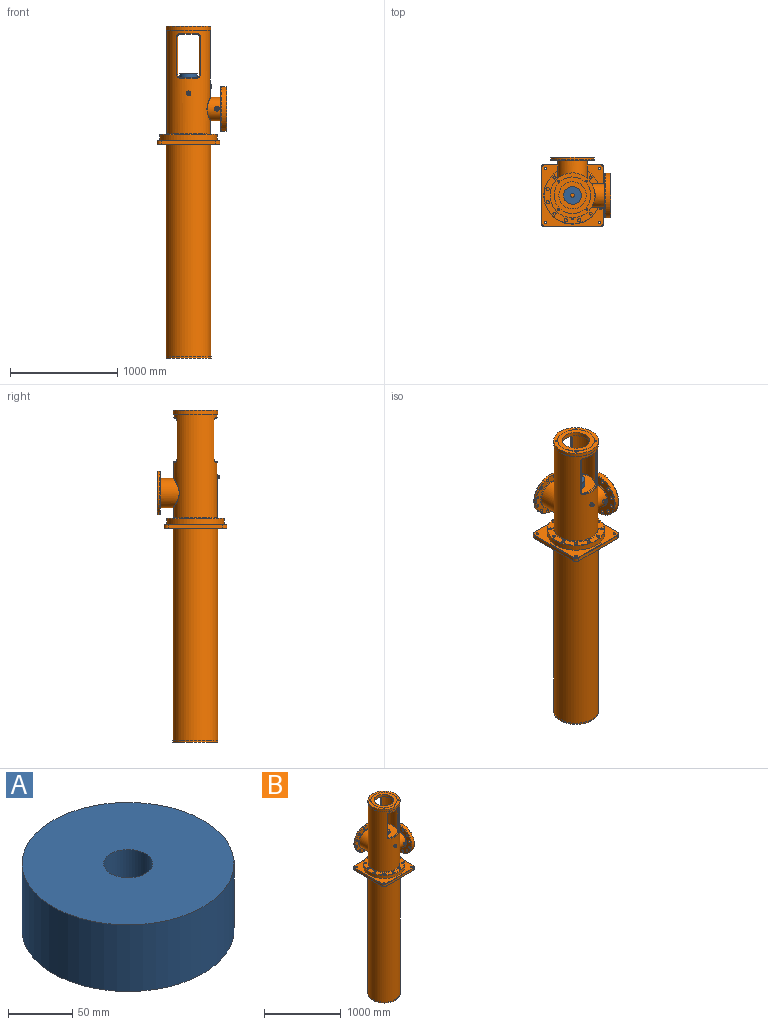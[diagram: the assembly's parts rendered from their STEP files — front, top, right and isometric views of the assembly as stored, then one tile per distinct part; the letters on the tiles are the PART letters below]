
ASSEMBLY  parts=2 mates=1
PART A: 4 faces, bbox 165.1x165.1x63.5 mm
  f0: cylinder r=19.05mm len=63.5mm, axis (0,0,-1), area 7600.6mm2, adj f2,f3
  f1: cylinder r=82.55mm len=165.1mm, axis (0,0,-1), area 32936mm2, adj f2,f3
  f2: plane 165.1x165.1mm, normal (0,0,1), area 20268.3mm2, adj f0,f1
  f3: plane 165.1x165.1mm, normal (0,0,-1), area 20268.3mm2, adj f0,f1
PART B: 185 faces, bbox 649.3x649.3x3098.8 mm
  f0: plane 194.31x194.31mm, normal (1,0,0), area 193.5mm2, adj f18,f177
  f1: cylinder r=127mm len=254mm, axis (0,1,0), area 157545.1mm2, adj f9,f181
  f2: cylinder r=203.2mm len=964.44mm, axis (0,0,-1), area 929917.2mm2, adj f35,f55,f56,f57,f58,f59,f60,f61
  f3: cylinder r=209.55mm len=419.1mm, axis (0,0,-1), area 45816.5mm2, adj f15,f154
  f4: plane 342.9x342.9mm, normal (0,0,1), area 41676.7mm2, adj f14,f153
  f5: cylinder r=12.7mm len=25.4mm, axis (0,1,0), area 1059.8mm2, adj f149,f151
  f6: cylinder r=7.3mm len=25.53mm, axis (0,-1,0), area 1168.4mm2, adj f7,f8
  f7: plane 19.05x19.05mm, normal (0,-1,0), area 117.5mm2, adj f6,f151
  f8: cylinder r=203.2mm len=14.61mm, axis (0,0,-1), area 167.6mm2, adj f6
  f9: cylinder r=184.15mm len=571.5mm, axis (0,0,-1), area 576329.1mm2, adj f1,f18,f74,f184
  f10: cylinder r=109.54mm len=219.08mm, axis (1,0,0), area 70763.1mm2, adj f32,f35,f150
  f11: plane 528.32x528.32mm, normal (0,0,1), area 75242.3mm2, adj f55,f75,f76,f77,f78,f79,f80,f81
  f12: cylinder r=184.15mm len=459.74mm, axis (0,0,-1), area 358288.8mm2, adj f36,f37,f38,f39,f40,f41,f42,f43
  f13: plane 358.14x358.14mm, normal (0,0,-1), area 50067.8mm2, adj f14,f54
  f14: cylinder r=127mm len=254mm, axis (0,0,-1), area 30402.4mm2, adj f4,f13
  f15: plane 419.1x419.1mm, normal (0,0,-1), area 1667.1mm2, adj f3,f56
  f16: cylinder r=209.55mm len=419.1mm, axis (1,0,0), area 57855.9mm2, adj f33,f34
  f17: plane 408.94x408.94mm, normal (-1,0,0), area 80571.2mm2, adj f20,f21,f22,f23,f24,f25,f26,f27
  f18: cylinder r=96.84mm len=198.97mm, axis (1,0,0), area 112354.4mm2, adj f0,f9,f148
  f19: plane 408.94x408.94mm, normal (1,0,0), area 64694.2mm2, adj f20,f21,f22,f23,f24,f25,f26,f27
  f20: cylinder r=15.88mm len=54.1mm, axis (1,0,0), area 5396.4mm2, adj f17,f19
  f21: cylinder r=15.88mm len=54.1mm, axis (1,0,0), area 5396.4mm2, adj f17,f19
  f22: cylinder r=15.88mm len=54.1mm, axis (1,0,0), area 5396.4mm2, adj f17,f19
  f23: cylinder r=15.88mm len=54.1mm, axis (1,0,0), area 5396.4mm2, adj f17,f19
  f24: cylinder r=15.88mm len=54.1mm, axis (1,0,0), area 5396.4mm2, adj f17,f19
  f25: cylinder r=15.88mm len=54.1mm, axis (1,0,0), area 5396.4mm2, adj f17,f19
  f26: cylinder r=15.88mm len=54.1mm, axis (1,0,0), area 5396.4mm2, adj f17,f19
  f27: cylinder r=15.88mm len=54.1mm, axis (1,0,0), area 5396.4mm2, adj f17,f19
  f28: cylinder r=15.88mm len=54.1mm, axis (1,0,0), area 5396.4mm2, adj f17,f19
  f29: cylinder r=15.88mm len=54.1mm, axis (1,0,0), area 5396.4mm2, adj f17,f19
  f30: cylinder r=15.88mm len=54.1mm, axis (1,0,0), area 5396.4mm2, adj f17,f19
  f31: cylinder r=15.88mm len=54.1mm, axis (1,0,0), area 5396.4mm2, adj f17,f19
  f32: torus R=114.62mm, axis (1,0,0), area 5584.5mm2, adj f10,f17
  f33: torus R=204.47mm, axis (1,0,0), area 10413.8mm2, adj f16,f19
  f34: torus R=204.47mm, axis (1,0,0), area 10413.8mm2, adj f16,f17
  f35: bspline ~229.29x223.71mm, area 4645.6mm2, adj f2,f10
  f36: cylinder r=25.4mm len=29.29mm, axis (0,-1,0), area 564.4mm2, adj f12,f37,f43,f67
  f37: plane 355.6x13.36mm, normal (1,0,0), area 4750.8mm2, adj f12,f36,f38,f65
  f38: cylinder r=25.4mm len=29.29mm, axis (0,-1,0), area 564.4mm2, adj f12,f37,f39,f66
  f39: plane 152.4x30.48mm, normal (0,0,-1), area 2190mm2, adj f12,f38,f40,f68
  f40: cylinder r=25.4mm len=29.29mm, axis (0,-1,0), area 564.4mm2, adj f12,f39,f41,f70
  f41: plane 355.6x13.36mm, normal (-1,0,0), area 4750.8mm2, adj f12,f40,f42,f72
  f42: cylinder r=25.4mm len=29.29mm, axis (0,-1,0), area 564.4mm2, adj f12,f41,f43,f71
  f43: plane 152.4x30.48mm, normal (0,0,1), area 2190mm2, adj f12,f36,f42,f69
  f44: plane 152.4x30.48mm, normal (0,0,1), area 2190mm2, adj f12,f45,f51,f60
  f45: cylinder r=25.4mm len=29.29mm, axis (0,-1,0), area 564.4mm2, adj f12,f44,f46,f58
  f46: plane 355.6x13.36mm, normal (-1,0,0), area 4750.8mm2, adj f12,f45,f47,f57
  f47: cylinder r=25.4mm len=29.29mm, axis (0,-1,0), area 564.4mm2, adj f12,f46,f48,f59
  f48: plane 152.4x30.48mm, normal (0,0,-1), area 2190mm2, adj f12,f47,f49,f61
  f49: cylinder r=25.4mm len=29.29mm, axis (0,-1,0), area 564.4mm2, adj f12,f48,f50,f63
  f50: plane 355.6x13.36mm, normal (1,0,0), area 4750.8mm2, adj f12,f49,f51,f64
  f51: cylinder r=25.4mm len=29.29mm, axis (0,-1,0), area 564.4mm2, adj f12,f44,f50,f62
  f52: plane 358.14x358.14mm, normal (0,0,1), area 80945.3mm2, adj f53,f165
  f53: torus R=179.07mm, axis (0,0,1), area 9140.3mm2, adj f12,f52
  f54: torus R=179.07mm, axis (0,0,1), area 9140.3mm2, adj f12,f13
  f55: torus R=208.28mm, axis (0,0,1), area 10280.5mm2, adj f2,f11
  f56: torus R=208.28mm, axis (0,0,1), area 10280.5mm2, adj f2,f15
  f57: cylinder r=5.08mm len=355.6mm, axis (0,0,-1), area 3864.7mm2, adj f2,f46,f58,f59
  f58: bspline ~36.12x33.55mm, area 439.7mm2, adj f2,f45,f57,f60
  f59: bspline ~36.12x33.55mm, area 439.7mm2, adj f2,f47,f57,f61
  f60: torus R=198.12mm, axis (0,0,1), area 1268.6mm2, adj f2,f44,f58,f62
  f61: torus R=198.12mm, axis (0,0,1), area 1268.6mm2, adj f2,f48,f59,f63
  f62: bspline ~36.12x33.55mm, area 439.7mm2, adj f2,f51,f60,f64
  f63: bspline ~36.12x33.55mm, area 439.7mm2, adj f2,f49,f61,f64
  f64: cylinder r=5.08mm len=355.6mm, axis (0,0,-1), area 3864.7mm2, adj f2,f50,f62,f63
  f65: cylinder r=5.08mm len=355.6mm, axis (0,0,-1), area 3864.7mm2, adj f2,f37,f66,f67
  f66: bspline ~36.12x33.55mm, area 439.7mm2, adj f2,f38,f65,f68
  f67: bspline ~36.12x33.55mm, area 439.7mm2, adj f2,f36,f65,f69
  f68: torus R=198.12mm, axis (0,0,1), area 1268.6mm2, adj f2,f39,f66,f70
  f69: torus R=198.12mm, axis (0,0,1), area 1268.6mm2, adj f2,f43,f67,f71
  f70: bspline ~36.12x33.55mm, area 439.7mm2, adj f2,f40,f68,f72
  f71: bspline ~36.12x33.55mm, area 439.7mm2, adj f2,f42,f69,f72
  f72: cylinder r=5.08mm len=355.6mm, axis (0,0,-1), area 3864.7mm2, adj f2,f41,f70,f71
  f73: cylinder r=266.7mm len=533.4mm, axis (0,0,-1), area 86403.8mm2, adj f116,f141
  f74: plane 368.3x368.3mm, normal (0,0,-1), area 100863.7mm2, adj f9,f166,f167,f168,f169,f170
  f75: cylinder r=14.29mm len=54.1mm, axis (0,0,-1), area 4856.8mm2, adj f11,f117
  f76: cylinder r=14.29mm len=54.1mm, axis (0,0,-1), area 4856.8mm2, adj f11,f118
  f77: cylinder r=14.29mm len=54.1mm, axis (0,0,-1), area 4856.8mm2, adj f11,f119
  f78: cylinder r=14.29mm len=54.1mm, axis (0,0,-1), area 4856.8mm2, adj f11,f120
  f79: cylinder r=14.29mm len=54.1mm, axis (0,0,-1), area 4856.8mm2, adj f11,f121
  f80: cylinder r=14.29mm len=54.1mm, axis (0,0,-1), area 4856.8mm2, adj f11,f122
  f81: cylinder r=14.29mm len=54.1mm, axis (0,0,-1), area 4856.8mm2, adj f11,f123
  f82: cylinder r=14.29mm len=54.1mm, axis (0,0,-1), area 4856.8mm2, adj f11,f124
  f83: cylinder r=14.29mm len=54.1mm, axis (0,0,-1), area 4856.8mm2, adj f11,f125
  f84: cylinder r=14.29mm len=54.1mm, axis (0,0,-1), area 4856.8mm2, adj f11,f126
  f85: cylinder r=14.29mm len=54.1mm, axis (0,0,-1), area 4856.8mm2, adj f11,f127
  f86: cylinder r=14.29mm len=54.1mm, axis (0,0,-1), area 4856.8mm2, adj f11,f128
  f87: cylinder r=136.53mm len=273.05mm, axis (0,1,0), area 120476.9mm2, adj f103,f106
  f88: plane 396.24x396.24mm, normal (0,-1,0), area 54236.7mm2, adj f90,f91,f92,f93,f94,f95,f96,f97
  f89: cylinder r=203.2mm len=406.4mm, axis (0,1,0), area 23349.1mm2, adj f104,f105
  f90: cylinder r=12.7mm len=28.45mm, axis (0,1,0), area 2270mm2, adj f88,f102
  f91: cylinder r=12.7mm len=28.45mm, axis (0,1,0), area 2270mm2, adj f88,f102
  f92: cylinder r=12.7mm len=28.45mm, axis (0,1,0), area 2270mm2, adj f88,f102
  f93: cylinder r=12.7mm len=28.45mm, axis (0,1,0), area 2270mm2, adj f88,f102
  f94: cylinder r=12.7mm len=28.45mm, axis (0,1,0), area 2270mm2, adj f88,f102
  f95: cylinder r=12.7mm len=28.45mm, axis (0,1,0), area 2270mm2, adj f88,f102
  f96: cylinder r=12.7mm len=28.45mm, axis (0,1,0), area 2270mm2, adj f88,f102
  f97: cylinder r=12.7mm len=28.45mm, axis (0,1,0), area 2270mm2, adj f88,f102
  f98: cylinder r=12.7mm len=28.45mm, axis (0,1,0), area 2270mm2, adj f88,f102
  f99: cylinder r=12.7mm len=28.45mm, axis (0,1,0), area 2270mm2, adj f88,f102
  f100: cylinder r=12.7mm len=28.45mm, axis (0,1,0), area 2270mm2, adj f88,f102
  f101: cylinder r=12.7mm len=28.45mm, axis (0,1,0), area 2270mm2, adj f88,f102
  f102: plane 396.24x396.24mm, normal (0,1,0), area 34860.2mm2, adj f90,f91,f92,f93,f94,f95,f96,f97
  f103: torus R=141.61mm, axis (0,-1,0), area 6937.6mm2, adj f87,f88
  f104: torus R=198.12mm, axis (0,-1,0), area 10095.4mm2, adj f89,f102
  f105: torus R=198.12mm, axis (0,-1,0), area 10095.4mm2, adj f88,f89
  f106: bspline ~283.27x276.36mm, area 5512.5mm2, adj f2,f87
  f107: plane 584.2x584.2mm, normal (0,0,-1), area 200522.9mm2, adj f108,f109,f110,f111,f112,f113,f114,f115
  f108: cylinder r=11.18mm len=38.1mm, axis (0,0,1), area 2675.4mm2, adj f107,f116
  f109: cylinder r=11.18mm len=38.1mm, axis (0,0,1), area 2675.4mm2, adj f107,f116
  f110: cylinder r=11.18mm len=38.1mm, axis (0,0,1), area 2675.4mm2, adj f107,f116
  f111: cylinder r=11.18mm len=38.1mm, axis (0,0,1), area 2675.4mm2, adj f107,f116
  f112: plane 508x35.56mm, normal (0,1,0), area 18064.5mm2, adj f107,f131,f132,f133
  f113: plane 508x35.56mm, normal (-1,0,0), area 18064.5mm2, adj f107,f130,f131,f137
  f114: plane 508x35.56mm, normal (0,-1,0), area 18064.5mm2, adj f107,f129,f130,f140
  f115: plane 508x35.56mm, normal (1,0,0), area 18064.5mm2, adj f107,f129,f132,f136
  f116: plane 579.12x579.12mm, normal (0,0,1), area 109266.9mm2, adj f73,f108,f109,f110,f111,f133,f134,f135
  f117: plane 28.58x28.58mm, normal (0,0,1), area 641.3mm2, adj f75
  f118: plane 28.58x28.58mm, normal (0,0,1), area 641.3mm2, adj f76
  f119: plane 28.58x28.58mm, normal (0,0,1), area 641.3mm2, adj f77
  f120: plane 28.58x28.58mm, normal (0,0,1), area 641.3mm2, adj f78
  f121: plane 28.58x28.58mm, normal (0,0,1), area 641.3mm2, adj f79
  f122: plane 28.58x28.58mm, normal (0,0,1), area 641.3mm2, adj f80
  f123: plane 28.58x28.58mm, normal (0,0,1), area 641.3mm2, adj f81
  f124: plane 28.58x28.58mm, normal (0,0,1), area 641.3mm2, adj f82
  f125: plane 28.58x28.58mm, normal (0,0,1), area 641.3mm2, adj f83
  f126: plane 28.58x28.58mm, normal (0,0,1), area 641.3mm2, adj f84
  f127: plane 28.58x28.58mm, normal (0,0,1), area 641.3mm2, adj f85
  f128: plane 28.58x28.58mm, normal (0,0,1), area 641.3mm2, adj f86
  f129: cylinder r=38.1mm len=38.1mm, axis (0,0,1), area 2128.2mm2, adj f107,f114,f115,f138
  f130: cylinder r=38.1mm len=38.1mm, axis (0,0,-1), area 2128.2mm2, adj f107,f113,f114,f139
  f131: cylinder r=38.1mm len=38.1mm, axis (0,0,1), area 2128.2mm2, adj f107,f112,f113,f135
  f132: cylinder r=38.1mm len=38.1mm, axis (0,0,-1), area 2128.2mm2, adj f107,f112,f115,f134
  f133: plane 508x2.54mm, normal (0,0.71,0.71), area 1824.8mm2, adj f112,f116,f134,f135
  f134: cone r=35.56mm half-angle=45deg, axis (0,0,-1), area 207.8mm2, adj f116,f132,f133,f136
  f135: cone r=35.56mm half-angle=45deg, axis (0,0,-1), area 207.8mm2, adj f116,f131,f133,f137
  f136: plane 508x2.54mm, normal (0.71,0,0.71), area 1824.8mm2, adj f115,f116,f134,f138
  f137: plane 508x2.54mm, normal (-0.71,0,0.71), area 1824.8mm2, adj f113,f116,f135,f139
  f138: cone r=35.56mm half-angle=45deg, axis (0,0,-1), area 207.8mm2, adj f116,f129,f136,f140
  f139: cone r=35.56mm half-angle=45deg, axis (0,0,-1), area 207.8mm2, adj f116,f130,f137,f140
  f140: plane 508x2.54mm, normal (0,-0.71,0.71), area 1824.8mm2, adj f114,f116,f138,f139
  f141: cone r=264.16mm half-angle=45deg, axis (0,0,-1), area 5990.7mm2, adj f11,f73
  f142: cylinder r=209.55mm len=1981.2mm, axis (0,0,1), area 2608530.1mm2, adj f107,f143
  f143: plane 420.42x420.42mm, normal (0,0,1), area 871mm2, adj f142,f145
  f144: plane 420.42x420.42mm, normal (0,0,-1), area 138822.1mm2, adj f145
  f145: cylinder r=210.21mm len=420.42mm, axis (0,0,1), area 16774.1mm2, adj f143,f144
  f146: cylinder r=12.7mm len=25.4mm, axis (0,1,0), area 464mm2, adj f150,f152
  f147: plane 19.05x19.05mm, normal (0,-1,0), area 117.5mm2, adj f148,f152
  f148: cylinder r=7.3mm len=30.55mm, axis (0,-1,0), area 1390.7mm2, adj f18,f147
  f149: bspline ~44.45x42.48mm, area 1451.1mm2, adj f2,f5
  f150: bspline ~44.46x40.91mm, area 1399.4mm2, adj f10,f146
  f151: torus R=9.53mm, axis (0,-1,0), area 361.8mm2, adj f5,f7
  f152: torus R=9.53mm, axis (0,-1,0), area 361.8mm2, adj f146,f147
  f153: cylinder r=171.45mm len=342.9mm, axis (0,0,1), area 3557.1mm2, adj f4,f154
  f154: plane 419.1x419.1mm, normal (0,0,1), area 44730.9mm2, adj f3,f153,f155,f157,f159,f161
  f155: cylinder r=8.33mm len=31.75mm, axis (0,0,1), area 1662.5mm2, adj f154,f156
  f156: cone r=0mm half-angle=59deg, axis (0,0,1), area 254.5mm2, adj f155
  f157: cylinder r=8.33mm len=31.75mm, axis (0,0,1), area 1662.5mm2, adj f154,f158
  f158: cone r=0mm half-angle=59deg, axis (0,0,1), area 254.5mm2, adj f157
  f159: cylinder r=8.33mm len=31.75mm, axis (0,0,1), area 1662.5mm2, adj f154,f160
  f160: cone r=0mm half-angle=59deg, axis (0,0,1), area 254.5mm2, adj f159
  f161: cylinder r=8.33mm len=31.75mm, axis (0,0,1), area 1662.5mm2, adj f154,f162
  f162: cone r=0mm half-angle=59deg, axis (0,0,1), area 254.5mm2, adj f161
  f163: cylinder r=76.2mm len=152.4mm, axis (0,0,1), area 60.8mm2, adj f164,f165
  f164: plane 152.4x152.4mm, normal (0,0,1), area 12569.9mm2, adj f163,f166,f167,f168,f169,f170
  f165: cone r=76.2mm half-angle=45deg, axis (0,0,1), area 2194.6mm2, adj f52,f163
  f166: cylinder r=41.27mm len=82.55mm, axis (0,0,1), area 5730.9mm2, adj f74,f164
  f167: cylinder r=5.04mm len=22.1mm, axis (0,0,1), area 700mm2, adj f74,f164
  f168: cylinder r=5.04mm len=22.1mm, axis (0,0,1), area 700mm2, adj f74,f164
  f169: cylinder r=5.04mm len=22.1mm, axis (0,0,1), area 700mm2, adj f74,f164
  f170: cylinder r=5.04mm len=22.1mm, axis (0,0,1), area 700mm2, adj f74,f164
  f171: cylinder r=9.53mm len=19.05mm, axis (-1,0,0), area 766.7mm2, adj f173,f174
  f172: cylinder r=15.88mm len=31.75mm, axis (-1,0,0), area 255.4mm2, adj f175,f176
  f173: plane 25.4x25.4mm, normal (1,0,0), area 221.7mm2, adj f171,f176
  f174: cylinder r=203.2mm len=19.05mm, axis (0,0,-1), area 285.1mm2, adj f171
  f175: bspline ~46.99x45.31mm, area 1340.8mm2, adj f2,f172
  f176: torus R=12.7mm, axis (1,0,0), area 461.3mm2, adj f172,f173
  f177: cylinder r=97.16mm len=194.31mm, axis (-1,0,0), area 969.1mm2, adj f0,f179
  f178: cylinder r=134.87mm len=269.75mm, axis (-1,0,0), area 1345.3mm2, adj f19,f179
  f179: plane 269.75x269.75mm, normal (1,0,0), area 27494.9mm2, adj f177,f178
  f180: cylinder r=161.93mm len=323.85mm, axis (0,-1,0), area 1615.1mm2, adj f102,f181
  f181: plane 323.85x323.85mm, normal (0,1,0), area 31700.9mm2, adj f1,f180
  f182: plane 400.05x400.05mm, normal (0,0,1), area 125695.1mm2, adj f183
  f183: cylinder r=200.03mm len=1981.2mm, axis (0,0,1), area 2489960.6mm2, adj f182,f184
  f184: plane 400.05x400.05mm, normal (0,0,-1), area 19159.9mm2, adj f9,f183
PLACE A t=(24.74,-221.73,124.58)mm
PLACE B t=(24.74,-221.73,127.88)mm
MATE fastened A.f0 <-> B.f2  axis (0,0,-1) through (24.74,-221.73,683.38)mm
